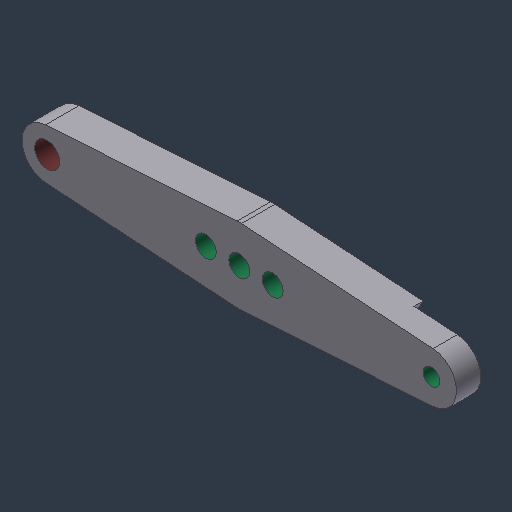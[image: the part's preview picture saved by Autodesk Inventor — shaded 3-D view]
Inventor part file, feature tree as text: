
AUTODESK INVENTOR PART (.ipt)
format: ipt  version: 2024.3 (Build 283343000, 343)  size: 142,336 bytes
history: native  units: mm (DEFAULTED — no unit token found)
features: sketch x5, hole x3, extrude x2
ambient origin geometry x8: Origin, YZ Plane, XZ Plane, XY Plane, X Axis, Y Axis, Z Axis, Center Point
bodies: Solid1 (feature_tree)
feature tree (10):
  extrude  "Extrusion1"  Depth=12.7mm
  hole  "Hole1"  [1 undecoded]
  hole  "Hole4"  [1 undecoded]
  sketch  "Sketch9"  dims[d34=9.525mm d35=19.05mm d36=9.779mm d37=6.35mm d38=14.3117mm d39=25.4mm d40=20.594885mm d41=6.35mm d42=19.05mm d43=6.858mm d44=1.9558mm d45=90.0deg d46=3.175mm d47=0.0mm d48=19.05mm d49=3.429mm d50=0.0mm]
  extrude  "Extrusion3"  TaperAngle=0.0deg  [1 undecoded]
  hole  "Hole5"  [1 undecoded]
  sketch  "Sketch2"  dims[d0=3.175mm d1=12.7mm]
  sketch  "Sketch3"  dims[d2=9.525mm d3=146.05mm]
  sketch  "Sketch7"  dims[d4=12.7mm d5=0.0mm d6=25.4mm]
  sketch  "Sketch8"  dims[d7=7.9502mm d8=19.05mm d9=8.4328mm d10=1.9558mm d11=90.0deg d12=25.4mm d13=20.594885mm]
note: 4 required parameter values undecoded (feature->parameter linkage not recoverable at this tier; creation-order binding heuristic only, values carry confidence <= 0.55)
